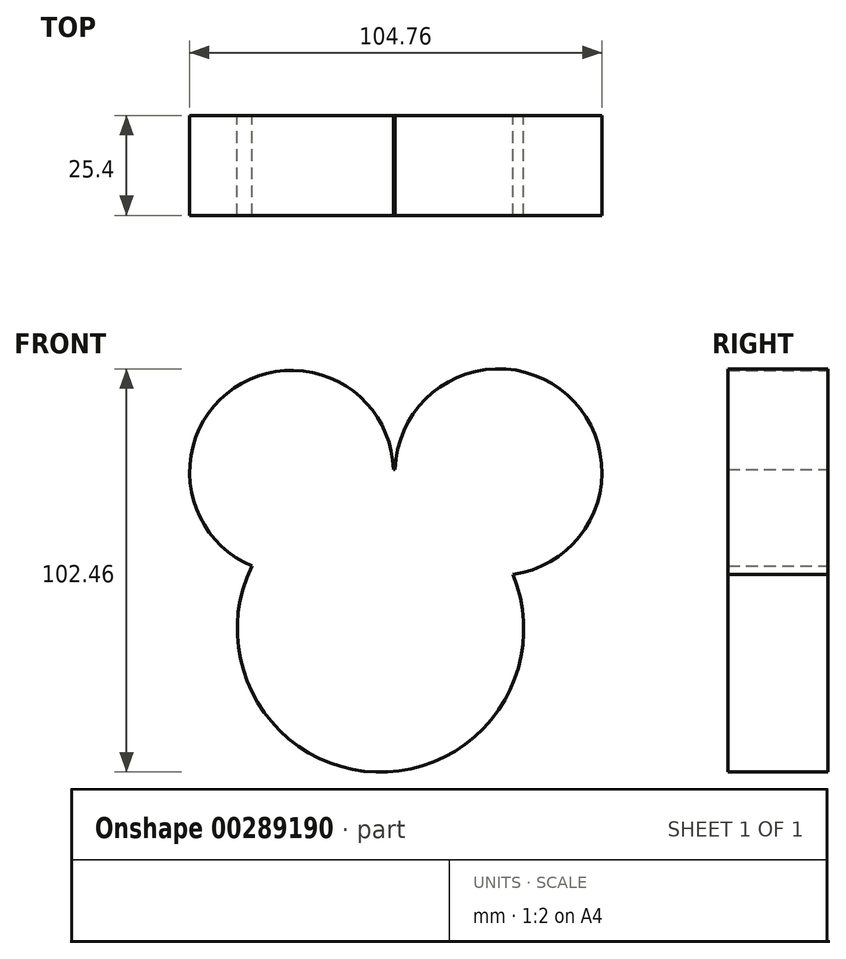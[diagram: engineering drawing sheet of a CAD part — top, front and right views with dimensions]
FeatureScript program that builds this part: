
annotation { "Feature Type Name" : "Feature", "Feature Type Description" : "" }
export const myFeature = defineFeature(function(context is Context, id is Id, definition is map)
    precondition{}
    {
        {
            var Q0;
            Q0=qCreatedBy(makeId("Front.planeOp"),FACE);
            var sketch = newSketch(context, id + "F0", { "sketchPlane" : qUnion([Q0])});
            skCircle(sketch, "E0", {"center": v(-62.93, 43.63) * mm, "radius": 25.9 * mm});
            skCircle(sketch, "E1", {"center": v(-10.32, 43.63) * mm, "radius": 26.26 * mm});
            skLineSegment(sketch, "E2.bottom", {"start": v(-59.24, 44.37) * mm, "end": v(-16.26, 44.37) * mm});
            skLineSegment(sketch, "E2.top", {"start": v(-59.24, 18.05) * mm, "end": v(-16.26, 18.05) * mm});
            skLineSegment(sketch, "E2.left", {"start": v(-59.24, 44.37) * mm, "end": v(-59.24, 18.05) * mm});
            skLineSegment(sketch, "E2.right", {"start": v(-16.26, 44.37) * mm, "end": v(-16.26, 18.05) * mm});
            skCircle(sketch, "E3", {"center": v(-40.31, 3.81) * mm, "radius": 36.38 * mm});
            skSolve(sketch);
        }
        {
            var Q0;
            Q0 = qSketchRegion(id + "F0", true);
            var Q1;
            {var subQ0=sQuery(id+"F0.wireOp",EDGE,"E2.top");var subQ1=sQuery(id+"F0.wireOp",EDGE,"E0");var subQ2=makeQuery(id+"F0.imprint","INTERSECT",VERTEX,{"derivedFrom":[subQ1,subQ0]});Q1=makeQuery(id+"F0.imprint","IMPRINT",FACE,{"disambiguationData":[TD([[makeQuery(id+"F0.imprint","IMPRINT",EDGE,{"disambiguationData":[TD([[subQ2,-1.0]])],"derivedFrom":subQ1}),-1.0]])]});}
            var Q2;
            {var subQ0=sQuery(id+"F0.wireOp",EDGE,"E2.top");var subQ1=sQuery(id+"F0.wireOp",EDGE,"E0");var subQ2=makeQuery(id+"F0.imprint","INTERSECT",VERTEX,{"derivedFrom":[subQ1,subQ0]});Q2=makeQuery(id+"F0.imprint","IMPRINT",FACE,{"disambiguationData":[TD([[makeQuery(id+"F0.imprint","IMPRINT",EDGE,{"disambiguationData":[TD([[subQ2,-1.0]])],"derivedFrom":subQ1}),1.0]])]});}
            var Q3;
            {var subQ1=sQuery(id+"F0.wireOp",EDGE,"E1");var subQ3=sQuery(id+"F0.wireOp",EDGE,"E3");var subQ4=makeQuery(id+"F0.imprint","INTERSECT",VERTEX,{"disambiguationData":[OD(1.0)],"derivedFrom":[subQ1,subQ3]});Q3=makeQuery(id+"F0.imprint","IMPRINT",FACE,{"disambiguationData":[TD([[makeQuery(id+"F0.imprint","IMPRINT",EDGE,{"disambiguationData":[TD([[subQ4,1.0]])],"derivedFrom":subQ3}),1.0]])]});}
            extrude(context, id + "F1", {"entities" : qUnion([Q0, Q1, Q2, Q3]), "depth" : 25.4 * mm});
        }
    });
